# Revit family: All-Lite_PEV-445_R17
name_source: partatom
category: Mechanical Equipment
revit_build: Autodesk Revit 2017 (Build: 20160225_1515(x64)
units: mm (PartAtom-declared; Revit-internal decimal feet)

## family parameters
Cut with Voids When Loaded = No
Host = Face
Part Type = Normal
Room Calculation Point = No
Round Connector Dimension = Use Diameter
Shared = No

## types (1)
- 38 1/2" x 38 1/2" x 18"
    Assembly Code = B3020300
    Blades = 45° ×x 0.081'' thick J- style.
    Corner = Boxed
    Curb Height = 36"
    Damper Model = SD-151 Class 1 Smoke Damper, Power Close, 2 x Internal Mount 120V AC Actuators.
    Damper Size = 26'' x 26''
    Default Elevation = 0"
    Depth = 38 1/2"
    Description = The PEV-445 extruded aluminum penthouse is designed for elevator shaft and gravity ventilator applications. The PEV-445
includes an SD-151, Class 1 smoke damper that fails open for
smoke evacuation.
    Frame = 4'' deep x 0.081'' thick channel.
    Height = 54"
    Louver Height = 13 3/4"
    Louver Width = 30 1/2"
    Manufacturer = All-Lite
    Material = Mill finish 6063-T5 extruded aluminum and 12 ga. galvanized steel curb.
    Model = PEV-445
    Modeled By = Commense Studio
    Penthouse Height = 18"
    Penthouse Size = See Dimensions
    Product URL = https://www.alllite.com
    Roof = 0.063'' 5052-H32 aluminum sheet with cross-break.
    Screen = 1/2'' x 0.063'' expanded and flattened aluminum.
    URL = https://www.alllite.com
    Width = 38 1/2"
    Window = 1/8'' thick annealed glass.

## geometry (parser evidence)
native form markers: Blend x4, Sweep x6
no freeform markers — native parametric forms only
